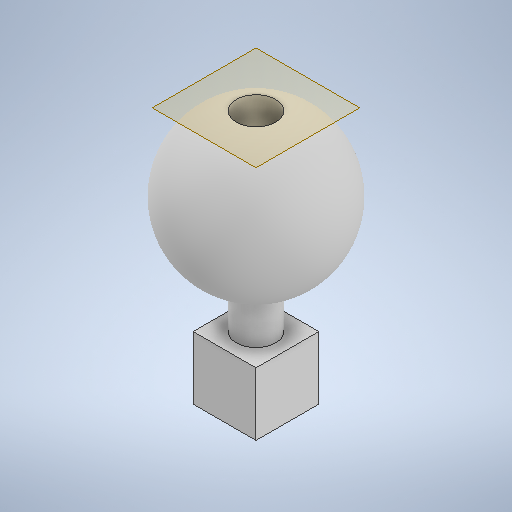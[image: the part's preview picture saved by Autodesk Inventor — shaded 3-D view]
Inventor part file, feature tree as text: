
AUTODESK INVENTOR PART (.ipt)
format: ipt  version: 2025.1 (Build 291241000, 241)  size: 313,856 bytes
history: native  units: mm
features: sketch x5, extrude x4, revolve x1, plane x1
ambient origin geometry x8: Origin, YZ Plane, XZ Plane, XY Plane, X Axis, Y Axis, Z Axis, Center Point
bodies: Volumenkörper1 (feature_tree)
feature tree (11):
  extrude  "Extrusion1"  Depth=6.0mm TaperAngle=0.0deg
  revolve  "Umdrehung1"
  plane  "Arbeitsebene1"
  extrude  "Extrusion3"  Depth=9.75mm
  extrude  "Extrusion5"  Depth=14.9mm
  extrude  "Extrusion4"  TaperAngle=90.0deg  [1 undecoded]
  sketch  "Skizze1"  dims[d0=5.0mm d1=6.0mm d2=0.0mm]
  sketch  "Skizze3"  dims[d6=19.5mm d7=9.75mm]
  sketch  "Skizze4"  dims[d8=9.75mm d10=14.9mm]
  sketch  "Skizze5"  dims[d11=0.0mm d12=90.0deg]
  sketch  "Skizze6"  dims[d13=5.0mm d14=14.5mm d15=0.0mm d16=3.3mm d17=25.0mm d18=0.0mm d21=4.0mm d22=4.0mm d23=8.0mm d24=4.0mm d25=8.0mm d26=0.0mm d30=0.5mm d31=0.872665mm d32=0.5mm d33=0.872665mm]
note: 1 required parameter value undecoded (feature->parameter linkage not recoverable at this tier; creation-order binding heuristic only, values carry confidence <= 0.55)
